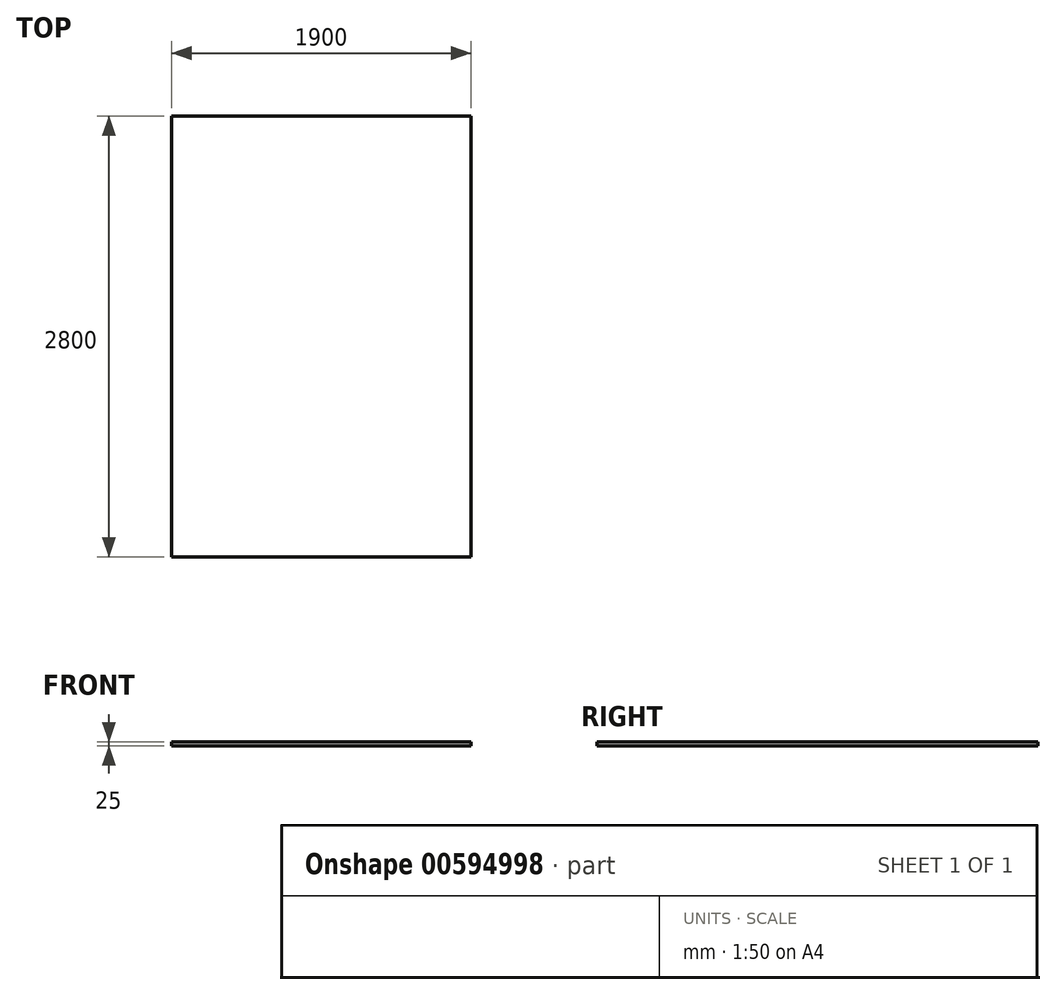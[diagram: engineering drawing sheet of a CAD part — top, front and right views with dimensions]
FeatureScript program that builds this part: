
annotation { "Feature Type Name" : "Feature", "Feature Type Description" : "" }
export const myFeature = defineFeature(function(context is Context, id is Id, definition is map)
    precondition{}
    {
        {
            var Q0;
            Q0=qCreatedBy(makeId("Top.planeOp"),FACE);
            var sketch = newSketch(context, id + "F0", { "sketchPlane" : qUnion([Q0])});
            skLineSegment(sketch, "E0.bottom", {"start": v(0, 0) * mm, "end": v(1900, 0) * mm});
            skLineSegment(sketch, "E0.top", {"start": v(0, 2800) * mm, "end": v(1900, 2800) * mm});
            skLineSegment(sketch, "E0.left", {"start": v(0, 0) * mm, "end": v(0, 2800) * mm});
            skLineSegment(sketch, "E0.right", {"start": v(1900, 0) * mm, "end": v(1900, 2800) * mm});
            skSolve(sketch);
        }
        {
            var Q0;
            Q0 = qSketchRegion(id + "F0", true);
            extrude(context, id + "F1", {"entities" : qUnion([Q0]), "depth" : 25 * mm, "offsetDistance" : 25 * mm});
        }
    });
